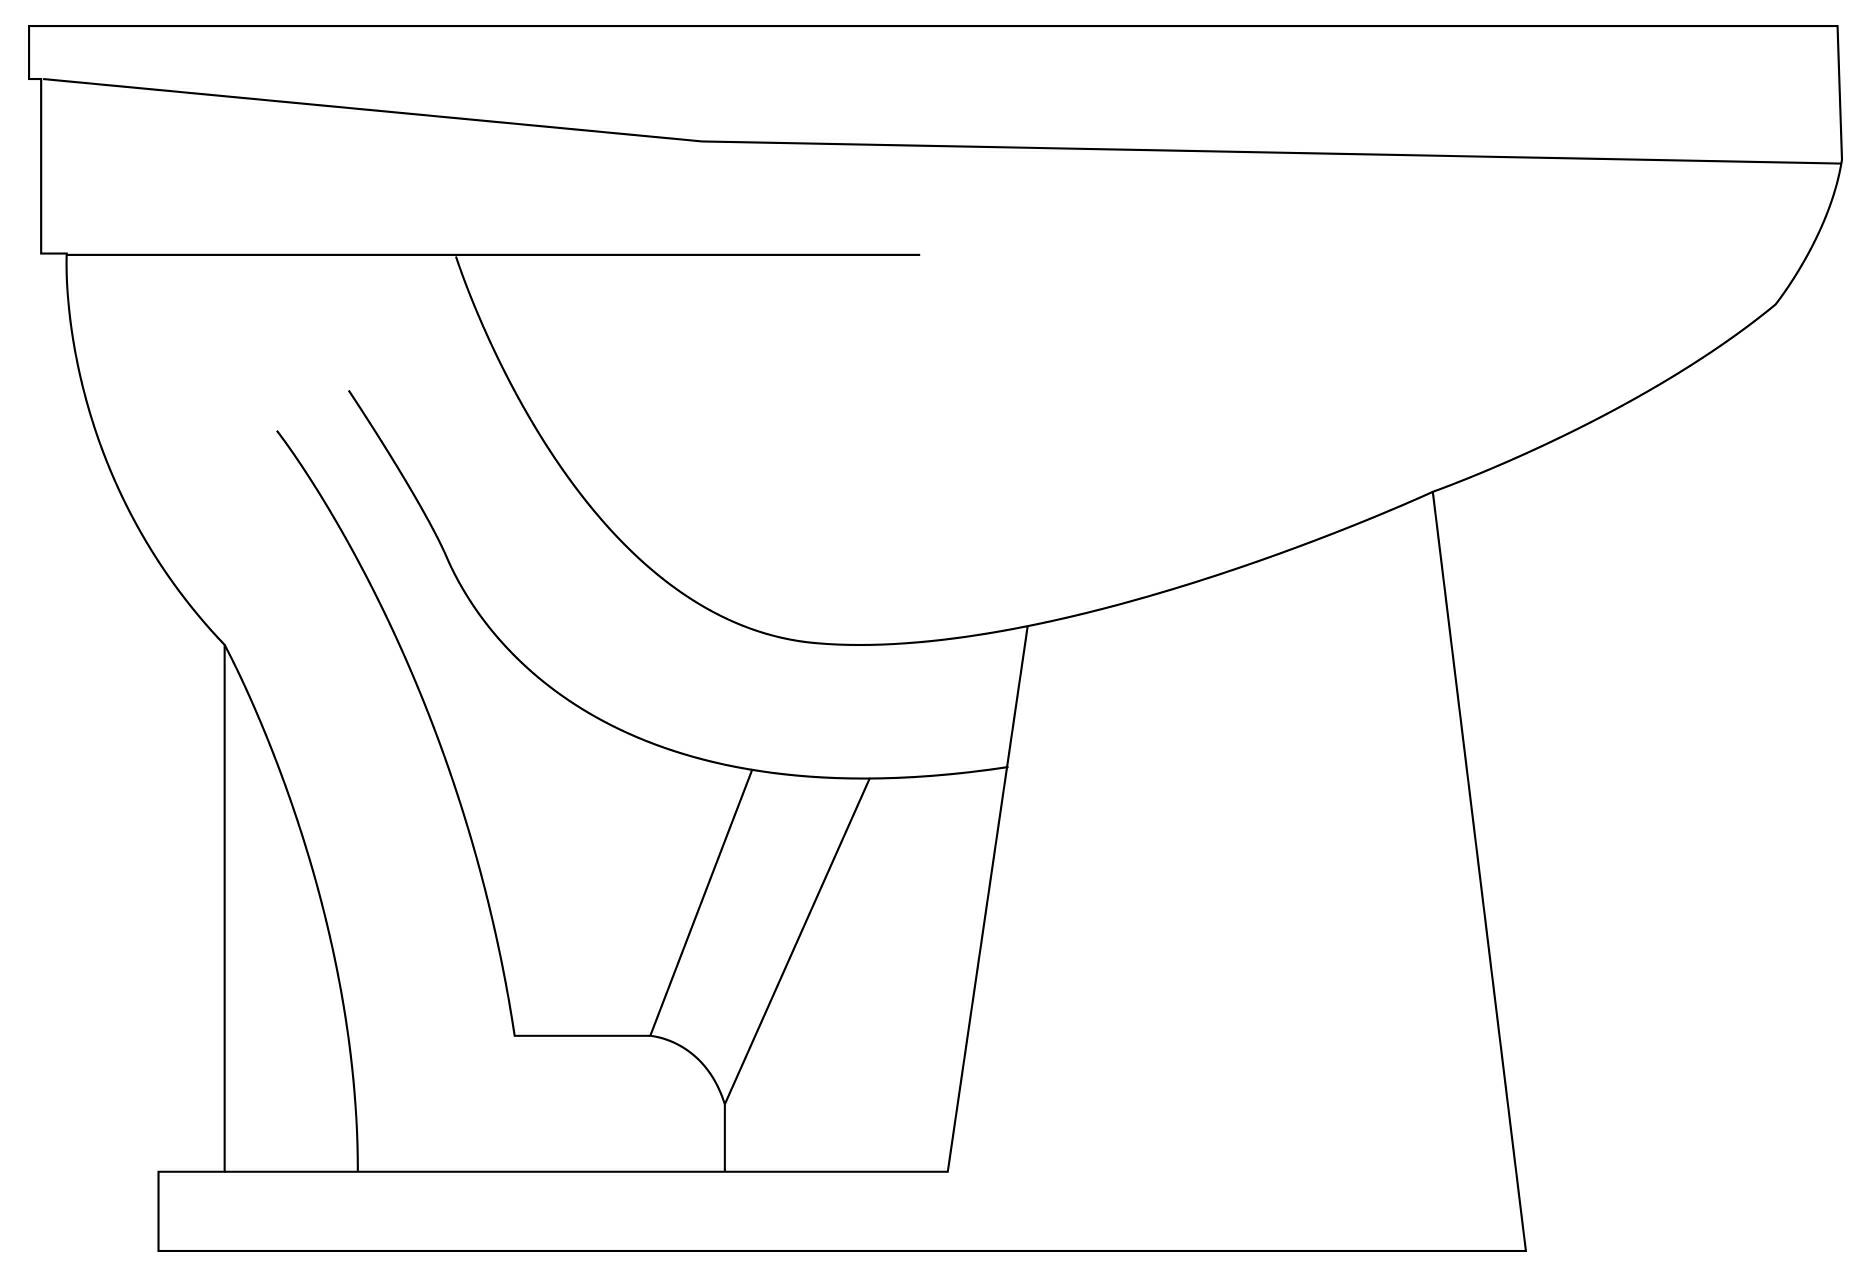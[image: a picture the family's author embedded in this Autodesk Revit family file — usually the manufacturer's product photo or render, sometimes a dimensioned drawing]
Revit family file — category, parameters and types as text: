
# Revit family: Adriatico entrada posterior
name_source: partatom
category: Aparatos sanitarios
revit_build: Autodesk Revit 2016 (Build: 20151007_0715(x64)
units: mm (PartAtom-declared; Revit-internal decimal feet)

## family parameters
Anfitrión = Muro
Compartido = No
Corte con vacíos al cargar = No
Cota de conector redondo = Diámetro de uso
Número OmniClass = 23.45.55.11
Punto de cálculo de habitación = No
Siempre vertical = Sí
Tipo de pieza = Normal
Título OmniClass = Sanitary Components

## types (1)
- Tipo 1
    Acabado = Brillante
    Altura Nominal = 430 mm
    Ancho Nominal = 397 mm  [stored 1.30249 ft]
    Características = Taza institucional de alta eficiencia en consumo de agua y alta capacidad de evacuación de descarga, perfecta para espacios comerciales, turismo, educación y salud.
    Color = Blanco
    Comentarios de tipo = Accesorio incluido: Racor metálico de 1 1/2" para fluxómetro
    Cumplimiento de Norma = ICONTEC NTC No. 920-1 ASME A112.19.2 CSA B 45.1 EPA WATERSENSE, NOM 009 / 010
    Código de montaje = D2010100
    Descripción 1 = Taza Adriatico AL de anillo cerrado de entrada posterior
    Descripción de la garantía = Garantía limitada de por vida
    Diámetro de conexión entrada = 1 1/2"
    Diámetro de conexión sanitaria = 4 "
    Fabricante = CORONA / COLCERAMICA
    Forma = Rectangular ovalada
    Imagen de tipo = <Ninguno>
    Longitud Nominal = 715 mm  [stored 2.3458 ft]
    Material = Ceramica_Corona_Blanco
    Material Secundario = Plastico_Corona_Blanco
    Material de Fabricación = Porcelana Sanitaria
    Modelo = Taza ADRIATICO AL anillo cerrado de entrada posterior
    Nombre = TAZA ADRIATICO AL ENTRADA POSTERIOR
    Nombre del Fabricante = CORONA / COLCERAMICA
    Número de modelo = 013191001
    Presión máxima = 80 PSI
    Presión mínima = 20 PSI
    Responsable de garantía partes = www.corona.com.co
    Tamaño = ( H x L x W ) 430 x 715 x 397
    Tipo de Activo = FIjo
    URL = https://www.corona.co

note: [stored X ft] marks values corroborated as IEEE doubles in the binary element streams (Revit-internal decimal feet)
